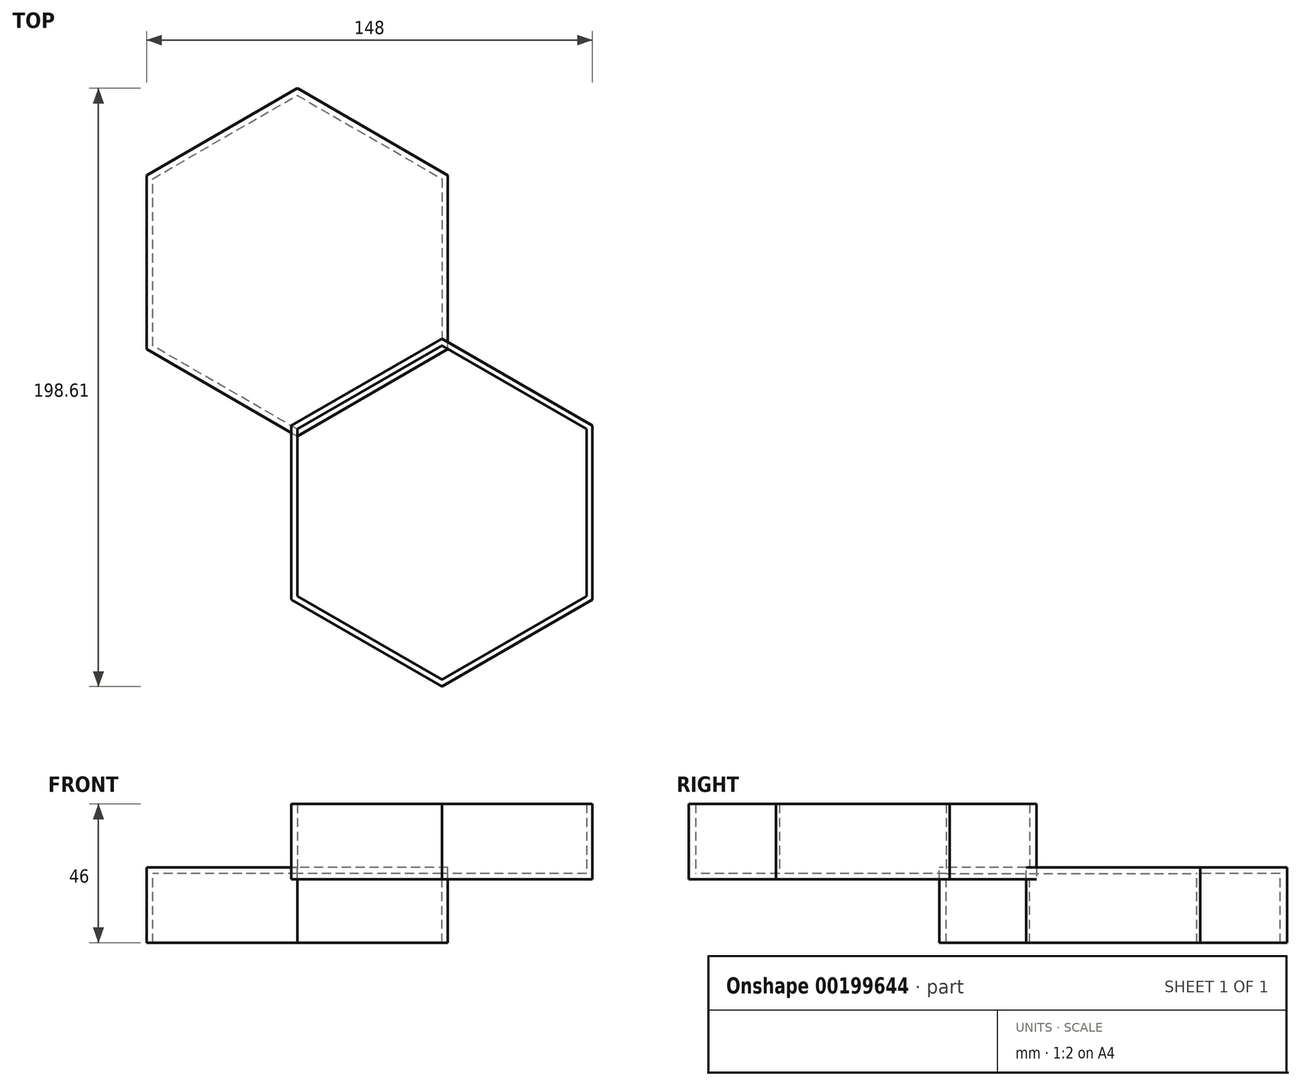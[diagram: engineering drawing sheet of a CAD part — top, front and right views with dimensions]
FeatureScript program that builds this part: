
annotation { "Feature Type Name" : "Feature", "Feature Type Description" : "" }
export const myFeature = defineFeature(function(context is Context, id is Id, definition is map)
    precondition{}
    {
        {
            var Q0;
            Q0=qCreatedBy(makeId("Top.planeOp"),FACE);
            var sketch = newSketch(context, id + "F0", { "sketchPlane" : qUnion([Q0])});
            skCircle(sketch, "E0.cCircle", {"center": v(0, 0) * mm, "radius": 50 * mm, "construction": true});
            skLineSegment(sketch, "E0.0", {"start": v(-50, -28.87) * mm, "end": v(-50, 28.87) * mm});
            skLineSegment(sketch, "E0.1", {"start": v(-50, 28.87) * mm, "end": v(0, 57.74) * mm});
            skLineSegment(sketch, "E0.2", {"start": v(0, 57.74) * mm, "end": v(50, 28.87) * mm});
            skLineSegment(sketch, "E0.3", {"start": v(50, 28.87) * mm, "end": v(50, -28.87) * mm});
            skLineSegment(sketch, "E0.4", {"start": v(50, -28.87) * mm, "end": v(0, -57.74) * mm});
            skLineSegment(sketch, "E0.5", {"start": v(0, -57.74) * mm, "end": v(-50, -28.87) * mm});
            skPoint(sketch, "E0.0.midPoint", {"position": v(-50, 0) * mm});
            skCircle(sketch, "E1.cCircle", {"center": v(0, 0) * mm, "radius": 48 * mm, "construction": true});
            skLineSegment(sketch, "E1.0", {"start": v(-48, -27.71) * mm, "end": v(-48, 27.71) * mm});
            skLineSegment(sketch, "E1.1", {"start": v(-48, 27.71) * mm, "end": v(0, 55.43) * mm});
            skLineSegment(sketch, "E1.2", {"start": v(0, 55.43) * mm, "end": v(48, 27.71) * mm});
            skLineSegment(sketch, "E1.3", {"start": v(48, 27.71) * mm, "end": v(48, -27.71) * mm});
            skLineSegment(sketch, "E1.4", {"start": v(48, -27.71) * mm, "end": v(0, -55.43) * mm});
            skLineSegment(sketch, "E1.5", {"start": v(0, -55.43) * mm, "end": v(-48, -27.71) * mm});
            skPoint(sketch, "E1.0.midPoint", {"position": v(-48, 0) * mm});
            skSolve(sketch);
        }
        {
            var Q0;
            Q0=makeQuery(id+"F0.imprint","IMPRINT",FACE,{"disambiguationData":[TD([[makeQuery(id+"F0.imprint","IMPRINT",EDGE,{"derivedFrom":sQuery(id+"F0.wireOp",EDGE,"E1.0")}),-1.0]])]});
            var Q1;
            Q1=makeQuery(id+"F0.imprint","IMPRINT",FACE,{"disambiguationData":[TD([[makeQuery(id+"F0.imprint","IMPRINT",EDGE,{"derivedFrom":sQuery(id+"F0.wireOp",EDGE,"E0.0")}),-1.0]])]});
            extrude(context, id + "F1", {"entities" : qUnion([Q0, Q1]), "depth" : 2 * mm, "offsetDistance" : 25 * mm});
        }
        {
            var Q0;
            Q0 = qSketchRegion(id + "F0", true);
            extrude(context, id + "F2", {"entities" : qUnion([Q0]), "operationType" : NewBodyOperationType.ADD, "depth" : 25 * mm, "offsetDistance" : 25 * mm});
        }
        {
            var Q0;
            Q0=makeQuery(id+"F1.opExtrude","SWEPT_BODY",BODY,{"disambiguationData":[OSD([sQuery(id+"F0.wireOp",EDGE,"E0.0"),sQuery(id+"F0.wireOp",EDGE,"E0.1"),sQuery(id+"F0.wireOp",EDGE,"E0.2"),sQuery(id+"F0.wireOp",EDGE,"E0.3"),sQuery(id+"F0.wireOp",EDGE,"E0.4"),sQuery(id+"F0.wireOp",EDGE,"E0.5")])]});
            var Q1;
            Q1=makeQuery(id+"F2.boolean.opBoolean","INTERSECT",EDGE,{"derivedFrom":[makeQuery(id+"F1.opExtrude","CAP_FACE",FACE,{"disambiguationData":[OSD([sQuery(id+"F0.wireOp",EDGE,"E0.0"),sQuery(id+"F0.wireOp",EDGE,"E0.1"),sQuery(id+"F0.wireOp",EDGE,"E0.2"),sQuery(id+"F0.wireOp",EDGE,"E0.3"),sQuery(id+"F0.wireOp",EDGE,"E0.4"),sQuery(id+"F0.wireOp",EDGE,"E0.5")])],"isStart":false}),makeQuery(id+"F2.opExtrude","SWEPT_FACE",FACE,{"disambiguationData":[OSD([sQuery(id+"F0.wireOp",EDGE,"E1.1")])]})]});
            transform(context, id + "F3", {"entities" : qUnion([Q0]), "transformType" : TransformType.ROTATION, "transformAxis" : qUnion([Q1]), "angle" : 180 * degree, "makeCopy" : true});
        }
    });
